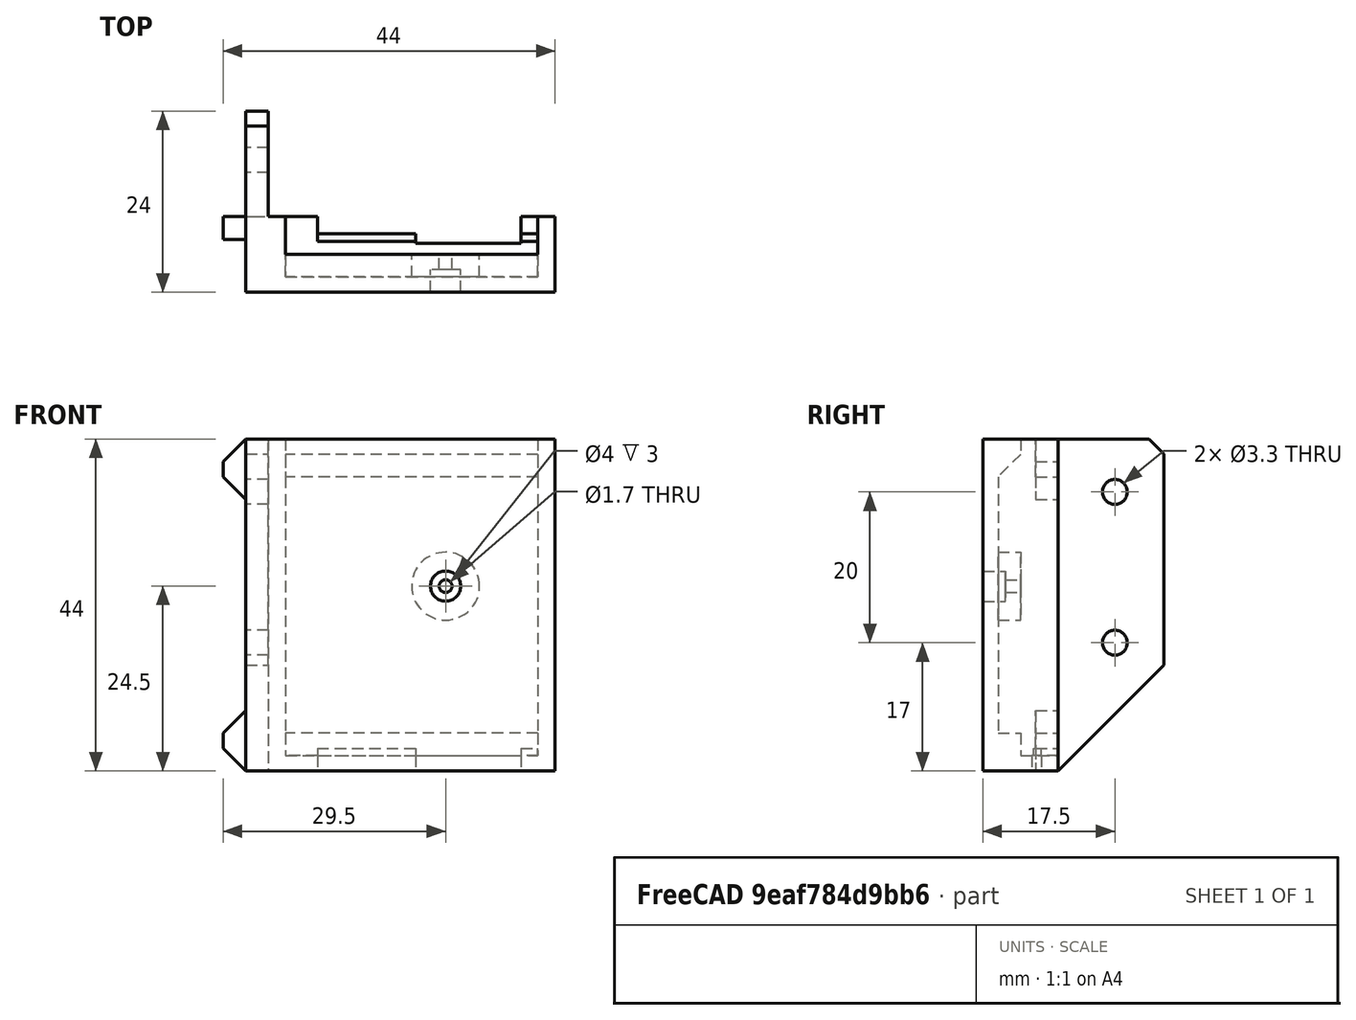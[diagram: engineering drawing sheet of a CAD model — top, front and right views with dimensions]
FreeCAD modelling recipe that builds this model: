
FCSTD DOCUMENT  (FreeCAD 0.18R16146 (Git))
Label: juice-plus-mount
License: All rights reserved
LicenseURL: http://en.wikipedia.org/wiki/All_rights_reserved
objects: Part::Box×10, Part::Cut×7, Part::Cylinder×5, Part::Chamfer×5, Part::MultiFuse×4
note: 31 computed .brp shape members not serialized (recipe doc carries the construction recipe); baked Part::Feature solids carry a one-line shape summary decoded from their .brp

FEATURE [Part::Box] Box002  label="Cube002"
  AttacherType = Attacher::AttachEngine3D
  Height = 10
  Length = 33.5
  Placement = pos=(-16.75,5,2) rot=(0,0,1;0rad)
  Width = 34
FEATURE [Part::Box] Box003  label="Cube003"
  AttacherType = Attacher::AttachEngine3D
  Height = 10
  Length = 14
  Placement = pos=(0.5,37,6.5) rot=(0,0,1;0rad)
  Width = 10
FEATURE [Part::Box] Box004  label="Cube004"
  AttacherType = Attacher::AttachEngine3D
  Height = 1
  Length = 13
  Placement = pos=(-12.5,41,6.75) rot=(0,0,1;0rad)
  Width = 3
FEATURE [Part::Box] Box005  label="Cube005"
  AttacherType = Attacher::AttachEngine3D
  Height = 10
  Length = 13
  Placement = pos=(-12.5,40,7.75) rot=(0,0,1;0rad)
  Width = 10
FEATURE [Part::Box] Box006  label="Cube006"
  AttacherType = Attacher::AttachEngine3D
  Height = 1
  Length = 3
  Placement = pos=(14.5,41,6.75) rot=(0,0,1;0rad)
  Width = 3
FEATURE [Part::Cylinder] Cylinder
  Angle = 360
  AttacherType = Attacher::AttachEngine3D
  Height = 3
  Placement = pos=(4.5,19.5,0) rot=(0,0,1;0rad)
  Radius = 2
FEATURE [Part::Cylinder] Cylinder001
  Angle = 360
  AttacherType = Attacher::AttachEngine3D
  Height = 5
  Placement = pos=(4.5,19.5,0) rot=(0,0,1;0rad)
  Radius = 4.5
FEATURE [Part::Box] Box001  label="Cube001"
  AttacherType = Attacher::AttachEngine3D
  Height = 10
  Length = 38
  Placement = pos=(-19,0,0) rot=(0,0,1;0rad)
  Width = 44
FEATURE [Part::Box] Box  label="Cube"
  AttacherType = Attacher::AttachEngine3D
  Height = 10
  Length = 33.5
  Placement = pos=(-16.75,0,5) rot=(0,0,1;0rad)
  Width = 42
FEATURE [Part::Cut] Cut
  Base = -> Box001
  Tool = -> Box
FEATURE [Part::Cut] Cut001
  Base = -> Cut
  Tool = -> Box002
FEATURE [Part::Cut] Cut002
  Base = -> Cut001
  Tool = -> Box005
FEATURE [Part::Cut] Cut003
  Base = -> Cut002
  Tool = -> Box003
FEATURE [Part::Chamfer] Chamfer
  Base = -> Cut003
  Edges = 1 edges r=2.99: [Edge36]
FEATURE [Part::Cylinder] Cylinder002
  Angle = 360
  AttacherType = Attacher::AttachEngine3D
  Height = 5
  Placement = pos=(4.5,19.5,0) rot=(0,0,1;0rad)
  Radius = 0.85
FEATURE [Part::MultiFuse] Fusion
  Shapes = -> [Cylinder001,Chamfer,Box004,Box006]
FEATURE [Part::Cut] Cut004
  Base = -> Fusion
  Tool = -> Cylinder002
FEATURE [Part::Cut] Cut005
  Base = -> Cut004
  Placement = pos=(21,-10,44) rot=(-1,0,0;1.5708rad)
  Tool = -> Cylinder
FEATURE [Part::Box] Box007  label="Cube007"
  AttacherType = Attacher::AttachEngine3D
  Height = 44
  Length = 3
  Placement = pos=(-1,-10,0) rot=(0,0,1;0rad)
  Width = 24
FEATURE [Part::Box] Box008  label="Cube008"
  AttacherType = Attacher::AttachEngine3D
  Height = 8
  Length = 4
  Placement = pos=(-6,-2,-7) rot=(0,0,1;0rad)
  Width = 3
FEATURE [Part::Box] Box009  label="Cube009"
  AttacherType = Attacher::AttachEngine3D
  Height = 8
  Length = 4
  Placement = pos=(-6,-2,44) rot=(0,0,1;0rad)
  Width = 3
FEATURE [Part::Chamfer] Chamfer001
  Base = -> Box009
  Edges = 2 edges r=3: [Edge2,Edge4]
  Placement = pos=(2,4,-8) rot=(0,0,1;0rad)
FEATURE [Part::Chamfer] Chamfer002
  Base = -> Box008
  Edges = 2 edges r=3: [Edge2,Edge4]
  Placement = pos=(2,4,7) rot=(0,0,1;0rad)
FEATURE [Part::Cylinder] Cylinder003
  Angle = 360
  AttacherType = Attacher::AttachEngine3D
  Height = 10
  Placement = pos=(5.2e-15,12.5,17) rot=(0,-1,0;1.5708rad)
  Radius = 1.65
FEATURE [Part::Cylinder] Cylinder004
  Angle = 360
  AttacherType = Attacher::AttachEngine3D
  Height = 10
  Placement = pos=(9e-15,12.5,37) rot=(0,-1,0;1.5708rad)
  Radius = 1.65
FEATURE [Part::MultiFuse] Fusion002
  Placement = pos=(0,-5,0) rot=(0,0,1;0rad)
  Shapes = -> [Chamfer001,Chamfer002]
FEATURE [Part::Chamfer] Chamfer003
  Base = -> Box007
  Edges = 1 edges r=14: [Edge11]
FEATURE [Part::MultiFuse] Fusion003
  Placement = pos=(5,-5,0) rot=(0,0,1;0rad)
  Shapes = -> [Cylinder003,Cylinder004]
FEATURE [Part::Chamfer] Chamfer004
  Base = -> Chamfer003
  Edges = 1 edges r=2: [Edge8]
FEATURE [Part::Cut] Cut006
  Base = -> Chamfer004
  Tool = -> Fusion003
FEATURE [Part::MultiFuse] Fusion004
  Shapes = -> [Fusion002,Cut006,Cut005]
